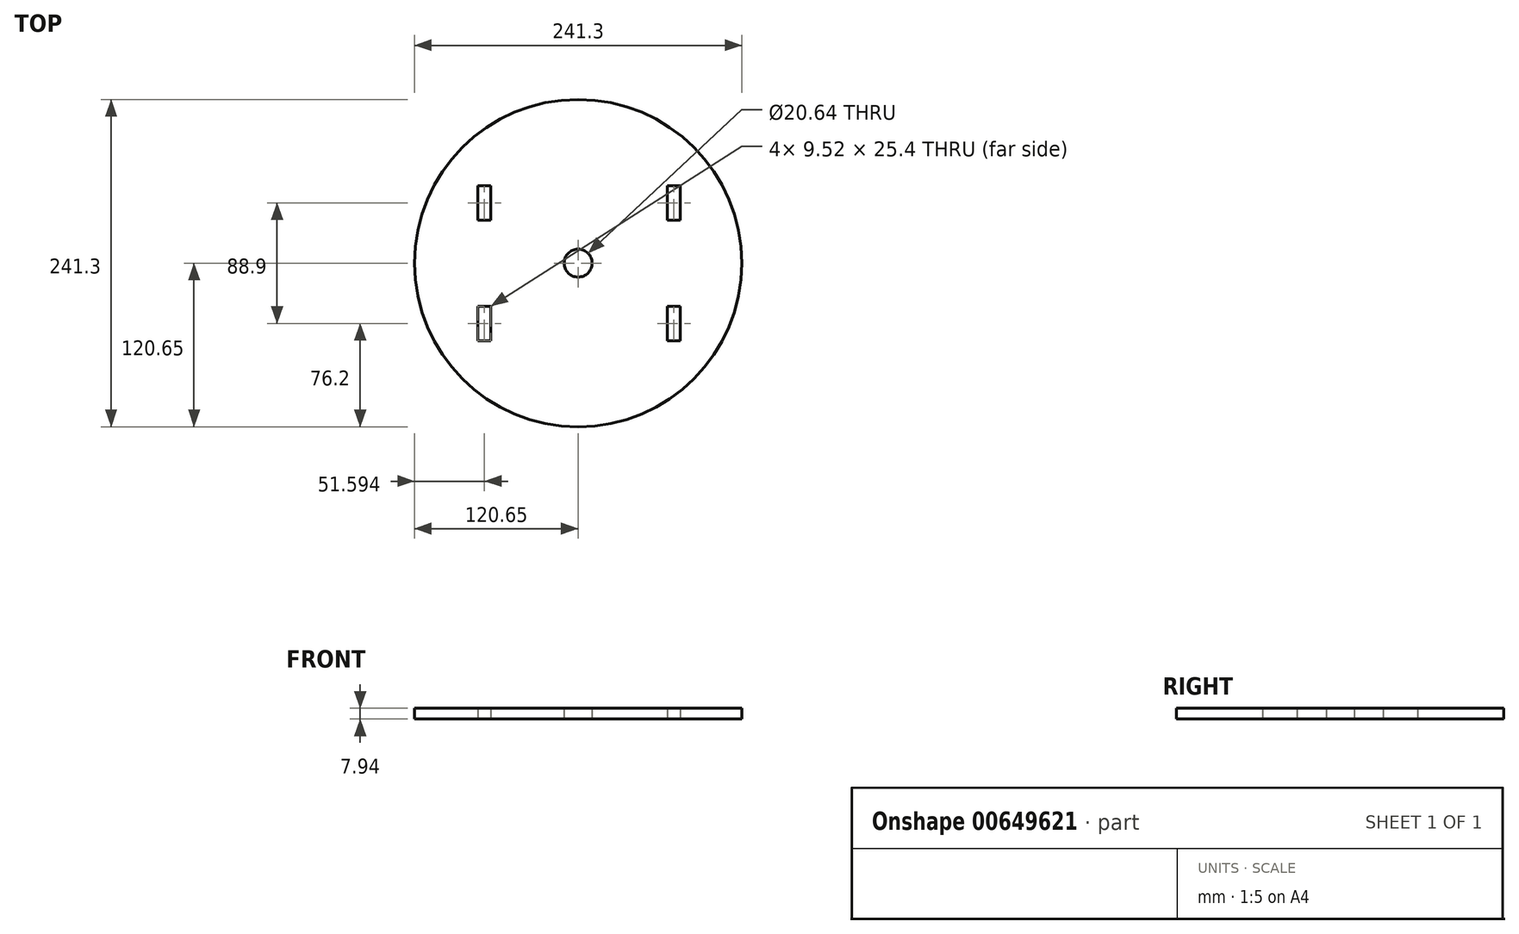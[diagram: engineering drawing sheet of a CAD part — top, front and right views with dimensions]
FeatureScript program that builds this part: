
annotation { "Feature Type Name" : "Feature", "Feature Type Description" : "" }
export const myFeature = defineFeature(function(context is Context, id is Id, definition is map)
    precondition{}
    {
        {
            var Q0;
            Q0=qCreatedBy(makeId("Top.planeOp"),FACE);
            var sketch = newSketch(context, id + "F0", { "sketchPlane" : qUnion([Q0])});
            skCircle(sketch, "E0", {"center": v(0, 0) * mm, "radius": 120.65 * mm});
            skLineSegment(sketch, "E1", {"start": v(-120.65, 0) * mm, "end": v(-59.47, 0) * mm, "construction": true});
            skLineSegment(sketch, "E2", {"start": v(59.47, 0) * mm, "end": v(120.65, 0) * mm, "construction": true});
            skLineSegment(sketch, "E3", {"start": v(-69.85, -98.37) * mm, "end": v(-69.85, 98.37) * mm, "construction": true});
            skLineSegment(sketch, "E4", {"start": v(69.85, -98.37) * mm, "end": v(69.85, 98.37) * mm, "construction": true});
            skLineSegment(sketch, "E5.bottom", {"start": v(-73.82, 57.15) * mm, "end": v(-64.3, 57.15) * mm});
            skLineSegment(sketch, "E5.top", {"start": v(-73.82, 31.75) * mm, "end": v(-64.3, 31.75) * mm});
            skLineSegment(sketch, "E5.left", {"start": v(-73.82, 57.15) * mm, "end": v(-73.82, 31.75) * mm});
            skLineSegment(sketch, "E5.right", {"start": v(-64.3, 57.15) * mm, "end": v(-64.3, 31.75) * mm});
            skLineSegment(sketch, "E6.bottom", {"start": v(-73.82, -31.75) * mm, "end": v(-64.3, -31.75) * mm});
            skLineSegment(sketch, "E6.top", {"start": v(-73.82, -57.15) * mm, "end": v(-64.3, -57.15) * mm});
            skLineSegment(sketch, "E6.left", {"start": v(-73.82, -31.75) * mm, "end": v(-73.82, -57.15) * mm});
            skLineSegment(sketch, "E6.right", {"start": v(-64.3, -31.75) * mm, "end": v(-64.3, -57.15) * mm});
            skLineSegment(sketch, "E7.bottom", {"start": v(65.88, 57.15) * mm, "end": v(75.4, 57.15) * mm});
            skLineSegment(sketch, "E7.top", {"start": v(65.88, 31.75) * mm, "end": v(75.4, 31.75) * mm});
            skLineSegment(sketch, "E7.left", {"start": v(65.88, 57.15) * mm, "end": v(65.88, 31.75) * mm});
            skLineSegment(sketch, "E7.right", {"start": v(75.4, 57.15) * mm, "end": v(75.4, 31.75) * mm});
            skLineSegment(sketch, "E8.bottom", {"start": v(65.88, -31.75) * mm, "end": v(75.4, -31.75) * mm});
            skLineSegment(sketch, "E8.top", {"start": v(65.88, -57.15) * mm, "end": v(75.4, -57.15) * mm});
            skLineSegment(sketch, "E8.left", {"start": v(65.88, -31.75) * mm, "end": v(65.88, -57.15) * mm});
            skLineSegment(sketch, "E8.right", {"start": v(75.4, -31.75) * mm, "end": v(75.4, -57.15) * mm});
            skCircle(sketch, "E9", {"center": v(0, 0) * mm, "radius": 10.32 * mm});
            skSolve(sketch);
        }
        {
            var Q0;
            Q0=qSketchRegion(id+"F0",true);
            extrude(context, id + "F1", {"entities" : qUnion([Q0]), "depth" : 7.94 * mm, "offsetDistance" : 25.4 * mm});
        }
    });
